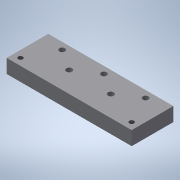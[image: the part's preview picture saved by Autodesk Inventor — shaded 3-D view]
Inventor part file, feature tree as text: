
AUTODESK INVENTOR PART (.ipt)
format: ipt  version: 2021 (Build 250183000, 183)  size: 161,792 bytes
history: native  units: in
note: dims shown in document units (in); Inventor stores cm internally (conversion verified against a paired STEP export)
features: sketch x6, extrude x5, hole x1
ambient origin geometry x8: Origin, YZ Plane, XZ Plane, XY Plane, X Axis, Y Axis, Z Axis, Center Point
bodies: Solid1 (feature_tree)
feature tree (12):
  extrude  "Extrusion1"  Depth=1.1811in
  extrude  "Extrusion2"  Depth=0.3937in
  extrude  "Extrusion4"  Depth=0.1614in
  extrude  "Extrusion5"  Depth=0.1969in
  extrude  "Extrusion6"  Depth=0.5906in
  hole  "Hole1"  [1 undecoded]
  sketch  "Sketch1"  dims[d0=3.5433in d5=1.1811in]
  sketch  "Sketch2"  dims[d6=0.3937in d7=0.0in d8=0.1614in]
  sketch  "Sketch4"  dims[d10=0.1614in d11=0.1614in]
  sketch  "Sketch5"  dims[d12=0.1969in d13=0.1969in]
  sketch  "Sketch6"  dims[d14=0.1969in d15=0.5906in]
  sketch  "Sketch8"  dims[d16=1.1811in d17=1.1811in d18=0.3937in d19=0.0in d26=0.2756in d28=0.2756in d29=0.2756in d30=0.1772in d31=0.0in d32=0.1654in d34=0.1654in d35=1.1811in d36=1.1811in d37=0.5906in d38=0.5906in d39=0.3937in d40=0.0in d41=0.2756in d43=0.2756in d44=0.1772in d45=0.0in d58=0.1969in d59=0.1969in d62=0.1969in d63=0.1969in d64=0.13in d65=0.328in d66=0.332in d67=0.0787in d68=0.5635in d69=0.4843in d70=0.0in]
note: 1 required parameter value undecoded (feature->parameter linkage not recoverable at this tier; creation-order binding heuristic only, values carry confidence <= 0.55)
